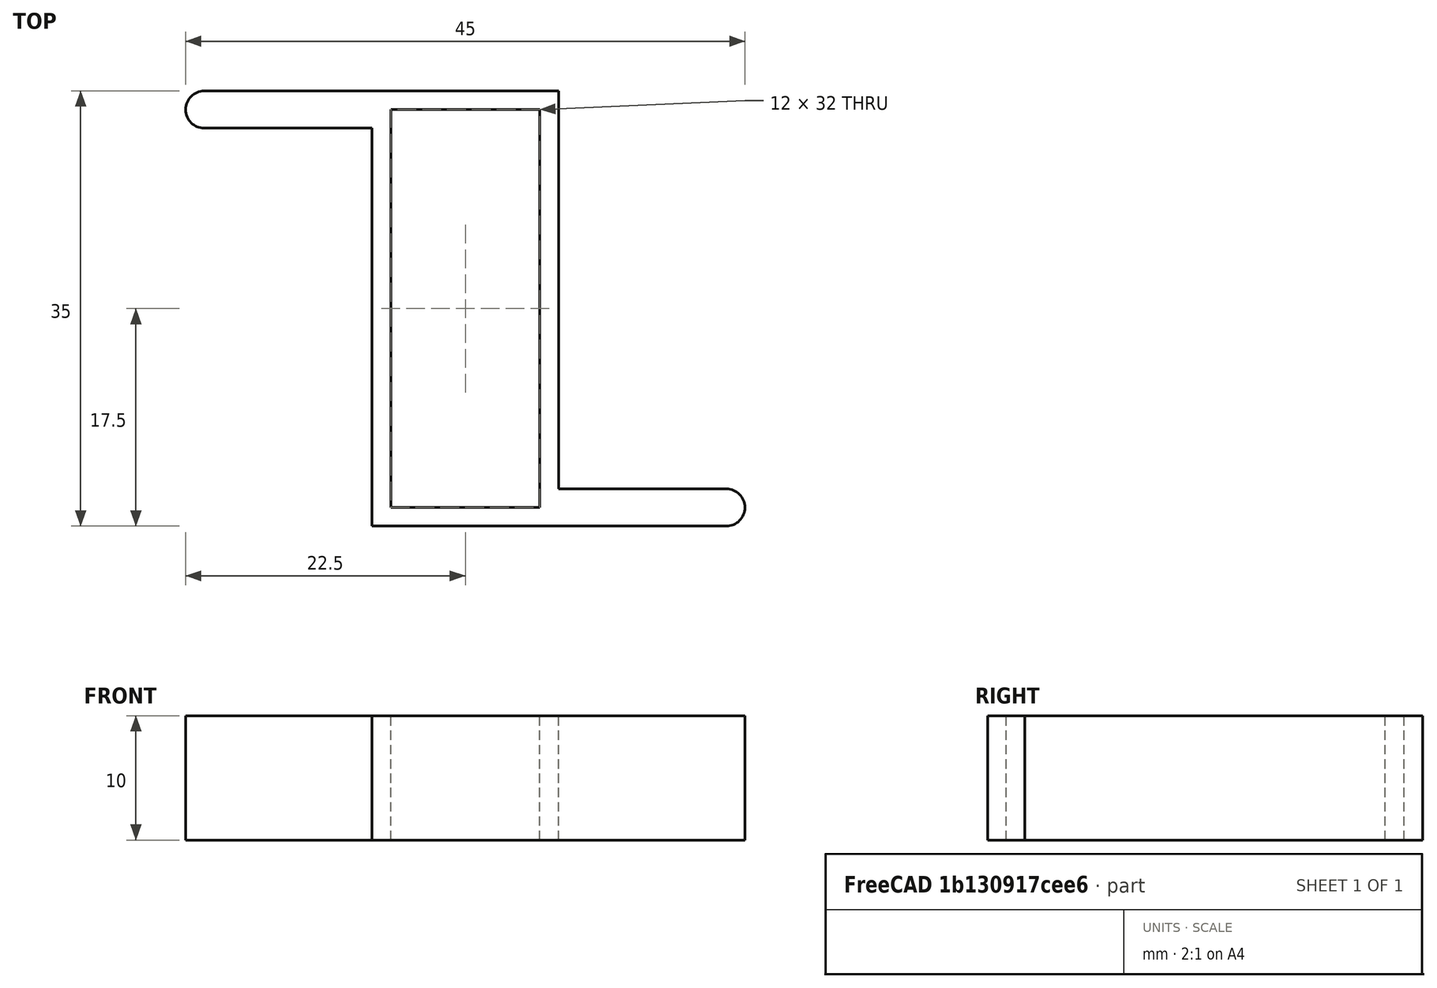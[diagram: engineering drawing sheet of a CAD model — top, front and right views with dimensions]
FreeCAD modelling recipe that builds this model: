
FCSTD DOCUMENT  (FreeCAD 0.17R13528 (Git))
Label: Perfil_R_5852
License: All rights reserved
LicenseURL: http://en.wikipedia.org/wiki/All_rights_reserved
objects: Spreadsheet::Sheet×1, Sketcher::SketchObject×1, PartDesign::Pad×1, PartDesign::Body×1
note: 4 computed .brp shape members not serialized (recipe doc carries the construction recipe); baked Part::Feature solids carry a one-line shape summary decoded from their .brp

FEATURE [Spreadsheet::Sheet] Spreadsheet  label="Tabla"
  cells = B1=Serie; C1=Serie_A; D1=Serie_B; E1=Serie_C; A2=Espesor; B2(Espesor_serie_A)=1.5; C2=1.5; D2=2; E2=2; A3=Alto; B3(Alto_serie_A)=35; C3=35; D3=50; E3=50; A4=Ancho; B4(Ancho_serie_A)=30; C4=30; D4=35; E4=60; A5=Ala; B5(Ala_serie_A)=15; C5=15; D5=15; E5=20
FEATURE [Sketcher::SketchObject] Sketch
  MapMode = 5
  Support = -> [XY_Plane]
  expr: Constraints[46] = Tabla.Ala_serie_A - Tabla.Espesor_serie_A
  expr: Constraints[43] = Tabla.Espesor_serie_A
  expr: Constraints[42] = Tabla.Ancho_serie_A - Tabla.Ala_serie_A
  expr: Constraints[24] = Tabla.Ancho_serie_A - Tabla.Ala_serie_A - 2 * Tabla.Espesor_serie_A
  expr: Constraints[20] = Tabla.Ancho_serie_A
  expr: Constraints[25] = Tabla.Espesor_serie_A
  expr: Constraints[26] = Tabla.Espesor_serie_A
  expr: Constraints[23] = Tabla.Alto_serie_A - 2 * Tabla.Espesor_serie_A
  expr: Constraints[19] = Tabla.Alto_serie_A
  sketch-geometry (16):
    g0: LineSegment StartX=1.50002 StartY=35 StartZ=0 EndX=30 EndY=35 EndZ=0
    g1: LineSegment StartX=30 StartY=35 StartZ=0 EndX=30 EndY=3 EndZ=0
    g2: LineSegment StartX=30 StartY=3 StartZ=0 EndX=43.5 EndY=3 EndZ=0
    g3: LineSegment StartX=43.5 StartY=0 StartZ=0 EndX=15 EndY=0 EndZ=0
    g4: LineSegment StartX=15 StartY=0 StartZ=0 EndX=15 EndY=32 EndZ=0
    g5: LineSegment StartX=15 StartY=32 StartZ=0 EndX=1.50002 EndY=32 EndZ=0
    g6: ArcOfCircle CenterX=43.5 CenterY=1.5 CenterZ=0 NormalX=0 NormalY=0 NormalZ=1 AngleXU=0 Radius=1.5 StartAngle=4.71239 EndAngle=7.85398
    g7: ArcOfCircle CenterX=1.5 CenterY=33.5 CenterZ=0 NormalX=0 NormalY=0 NormalZ=1 AngleXU=0 Radius=1.5 StartAngle=1.57079 EndAngle=4.7124
    g8: LineSegment StartX=16.5 StartY=33.5 StartZ=0 EndX=28.5 EndY=33.5 EndZ=0
    g9: LineSegment StartX=28.5 StartY=33.5 StartZ=0 EndX=28.5 EndY=1.5 EndZ=0
    g10: LineSegment StartX=28.5 StartY=1.5 StartZ=0 EndX=16.5 EndY=1.5 EndZ=0
    g11: LineSegment StartX=16.5 StartY=1.5 StartZ=0 EndX=16.5 EndY=33.5 EndZ=0
    g12: LineSegment [constr] StartX=15 StartY=0 StartZ=0 EndX=45 EndY=0 EndZ=0
    g13: LineSegment [constr] StartX=45 StartY=0 StartZ=0 EndX=45 EndY=35 EndZ=0
    g14: LineSegment [constr] StartX=45 StartY=35 StartZ=0 EndX=15 EndY=35 EndZ=0
    g15: LineSegment [constr] StartX=15 StartY=35 StartZ=0 EndX=15 EndY=0 EndZ=0
  constraints (47):
    c: Equal(g4,g1)
    c: Equal(g0,g3)
    c: Equal(g7,g6)
    c: Coincident(g0,g7)
    c: Coincident(g5,g7)
    c: Coincident(g4,g5)
    c: Coincident(g8,g11)
    c: Coincident(g8,g9)
    c: Coincident(g0,g1)
    c: Coincident(g3,g4)
    c: Coincident(g3,g12)
    c: Coincident(g3,g15)
    c: Coincident(g10,g11)
    c: Coincident(g9,g10)
    c: Coincident(g1,g2)
    c: Vertical(g1)
    c: Vertical(g9)
    c: Vertical(g4)
    c: Vertical(g11)
    c: DistanceY(g13,g13) = 35
    c: DistanceX(g14,g14) = 30
    c: Tangent(g7,g-2)
    c: Tangent(g6,g13)
    c: DistanceY(g11,g11) = 32
    c: DistanceX(g8,g8) = 12
    c: DistanceX(g3,g10) = 1.5
    c: DistanceY(g3,g10) = 1.5
    c: PointOnObject(g0,g14)
    c: PointOnObject(g3,g-1)
    c: PointOnObject(g0,g14)
    c: Coincident(g13,g14)
    c: Coincident(g14,g15)
    c: Coincident(g12,g13)
    c: Horizontal(g14)
    c: Horizontal(g12)
    c: Vertical(g15)
    c: Vertical(g13)
    c: Horizontal(g8)
    c: Horizontal(g10)
    c: Horizontal(g2)
    c: Horizontal(g5)
    c: Horizontal(g3)
    c: DistanceX(g14,g0) = 15
    c: Radius(g7) = 1.5
    c: Tangent(g6,g2) = 1.5708
    c: Tangent(g3,g6) = 1.5708
    c: DistanceX(g5,g5) = 13.5
FEATURE [PartDesign::Pad] Pad
  Length = 10
  Length2 = 100
  Profile = -> Sketch
  Refine = true
  Type = 0
FEATURE [PartDesign::Body] Body
  Group = -> [Sketch,Pad]
  Origin = -> Origin
  Tip = -> Pad
